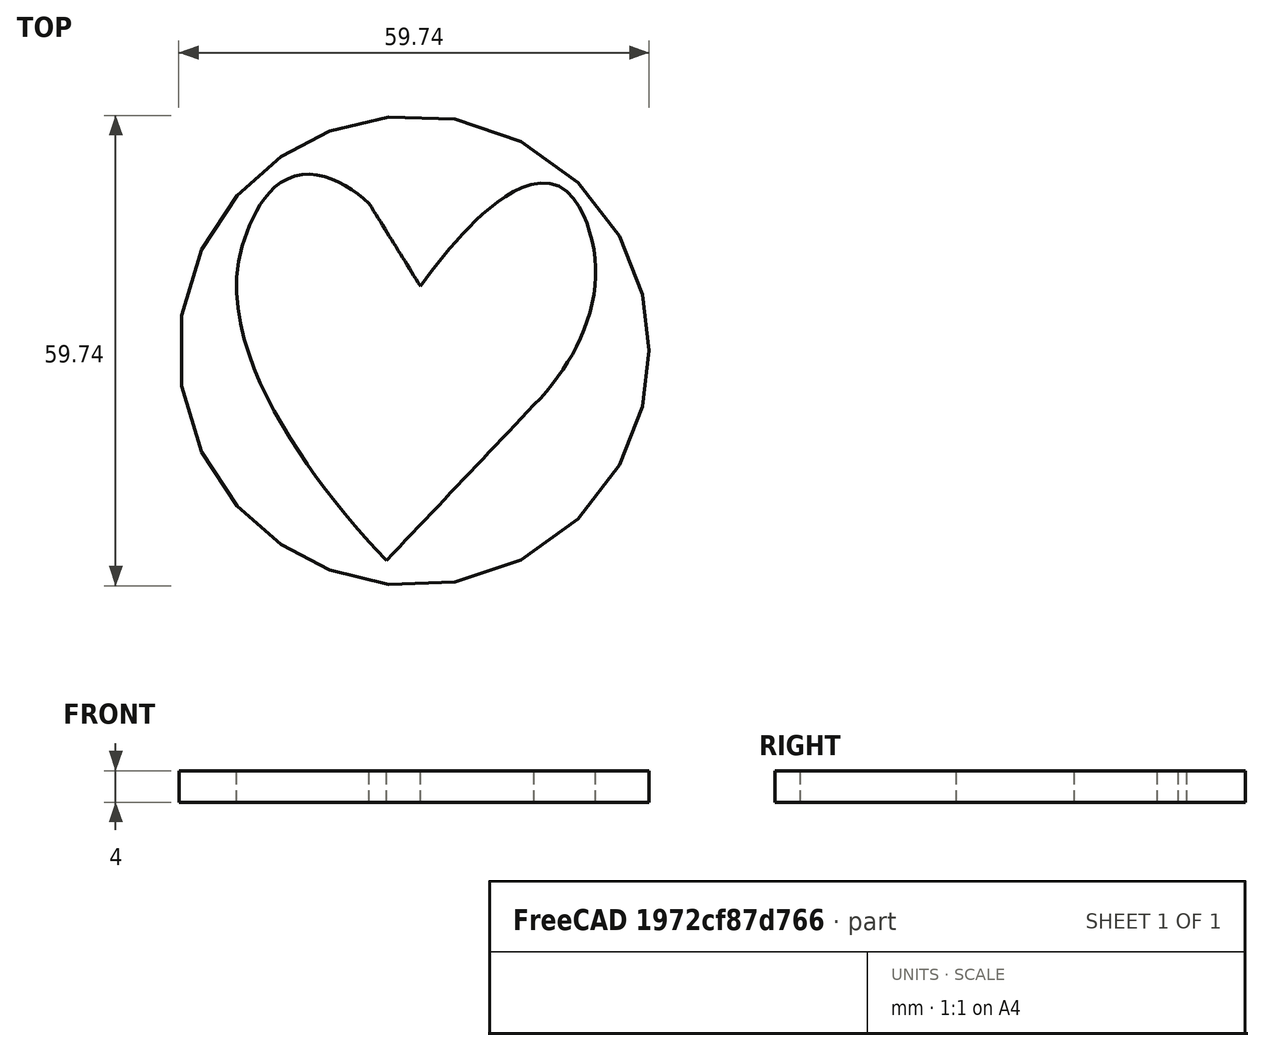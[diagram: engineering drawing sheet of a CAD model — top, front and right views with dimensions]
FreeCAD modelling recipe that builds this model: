
FCSTD DOCUMENT  (FreeCAD 1.0R38806 (Git))
Label: corazon_medallon
License: All rights reserved
LicenseURL: https://en.wikipedia.org/wiki/All_rights_reserved
objects: Part::Feature×2, Part::Extrusion×2, Part::Cut×1
note: 5 computed .brp shape members not serialized (recipe doc carries the construction recipe); baked Part::Feature solids carry a one-line shape summary decoded from their .brp

FEATURE [Part::Feature] path1153
  shape: bbox 54.17 x 56.83 x 2e-07 mm, 1 faces, 0 solids (baked)
FEATURE [Part::Feature] path1693
  Placement = pos=(83.313,-54.0551,0) rot=(0,0,1;0rad)
  shape: bbox 59.73 x 59.73 x 2e-07 mm, 1 faces, 0 solids (baked)
FEATURE [Part::Extrusion] Extrude
  Base = -> path1693
  Dir = (0,0,1)
  DirMode = 0
  FaceMakerClass = Part::FaceMakerBullseye
  FaceMakerMode = 3
  LengthFwd = 4
  LengthRev = 0
  Solid = false
  Symmetric = false
FEATURE [Part::Extrusion] Extrude001
  Base = -> path1153
  Dir = (0,0,1)
  DirMode = 0
  FaceMakerClass = Part::FaceMakerBullseye
  FaceMakerMode = 3
  LengthFwd = 6
  LengthRev = 0
  Placement = pos=(-81,-2,-1) rot=(0,0,1;0rad)
  Solid = false
  Symmetric = false
FEATURE [Part::Cut] Cut
  Base = -> Extrude
  Refine = true
  Tool = -> Extrude001
